# Revit family: Vents_VCUN_Eng
name_source: partatom
category: Mechanical Equipment
units: mm (PartAtom-declared; Revit-internal decimal feet)

## family parameters
Always vertical = Yes
Classification = None
Cut with Voids When Loaded = No
Part Type = Normal
Room Calculation Point = No
Round Connector Dimension = Use Diameter
Shared = No
Work Plane-Based = No

## types (31) — shared parameters
00_20_Manufacturer = Vents
00_20_Name = Centrifugal fan in scroll casing
Casing Material = Metal, painted, blue, matte RAL 5007
Frequency = 50 Hz
Hd = 450 mm
Load Classification = HVAC
Maintenance zone material = <By Category>
Manufacturer = Vents
Number of Fase = 3
Temperature of moving air = 60°С
URL = https://ventilation-system.com
Voltage = 400 V
X2 = 12 mm  [stored 0.0393701 ft]
zero-valued in all types: Default Elevation

## per-type parameters (varying)
- VCUN 500х229-11,0-4: 00_20_Type=VCUN 500х229-11,0-4; Amperage=24 A; B=860 mm; D=500 mm; Diameter=500 mm; F=48 mm  [stored 0.15748 ft]; Frame=Frame VCUN : Frame _500/11; Frame corner=63 mm  [stored 0.206693 ft]; H=1115 mm; H1=390 mm; H2=341 mm; H3=534 mm; Height=1115 mm; Hy=355 mm; L=761 mm; L1=401 mm; L2=353 mm; Length=824 mm; Ly=355 mm; Maximum Air Flow=17250.0 m³/h; Motor=Motor : Motor 11 kW; Power=11000 W; R=250 mm; R1=464 mm; R2=450 mm; R3=340 mm; Weight=107.00 kg; Width=860 mm; X1=483 mm; X3=250 mm; X4=365 mm; Y1=15 mm  [stored 0.0492126 ft]; Y2=330 mm; Y3=190 mm; Y4=531 mm; d=11 mm  [stored 0.0360892 ft]; f=24 mm  [stored 0.0787402 ft]; l=177 mm; r1=31 mm  [stored 0.101706 ft]; r2=145 mm
- VCUN 140х74-0,37-2: 00_20_Type=VCUN 140х74-0,37-2; Amperage=1 A; B=242 mm; D=140 mm; Diameter=140 mm; F=30 mm  [stored 0.0984252 ft]; Frame=Frame VCUN : Frame _140/0.37; Frame corner=35 mm  [stored 0.114829 ft]; H=323 mm; H1=125 mm; H2=92 mm; H3=144 mm; Height=323 mm; Hy=100 mm; L=309 mm; L1=125 mm; L2=95 mm; Length=344 mm; Ly=100 mm; Maximum Air Flow=710.0 m³/h; Motor=Motor : Motor 0.37 kW; Power=370 W; R=70 mm; R1=130 mm; R2=140 mm; R3=100 mm; Weight=9.30 kg; Width=242 mm; X1=130 mm; X3=75 mm; X4=102 mm; Y1=15 mm  [stored 0.0492126 ft]; Y2=95 mm; Y3=57 mm  [stored 0.187008 ft]; Y4=149 mm; d=8 mm  [stored 0.0262467 ft]; f=15 mm  [stored 0.0492126 ft]; l=48 mm  [stored 0.15748 ft]; r1=9 mm  [stored 0.0295276 ft]; r2=39 mm  [stored 0.127953 ft]
- VCUN 160х74-0,55-4: 00_20_Type=VCUN 160х74-0,55-4; Amperage=2 A; B=277 mm; D=160 mm; Diameter=160 mm; F=30 mm  [stored 0.0984252 ft]; Frame=Frame VCUN : Frame _160/0.55; Frame corner=35 mm  [stored 0.114829 ft]; H=373 mm; H1=134 mm; H2=106 mm; H3=173 mm; Height=373 mm; Hy=112 mm; L=356 mm; L1=134 mm; L2=104 mm; Length=391 mm; Ly=112 mm; Maximum Air Flow=750.0 m³/h; Motor=Motor : Motor 0.55 kW; Power=550 W; R=80 mm; R1=150 mm; R2=140 mm; R3=110 mm; Weight=12.70 kg; Width=277 mm; X1=150 mm; X3=85 mm; X4=118 mm; Y1=15 mm  [stored 0.0492126 ft]; Y2=110 mm; Y3=64 mm  [stored 0.209974 ft]; Y4=170 mm; d=8 mm  [stored 0.0262467 ft]; f=15 mm  [stored 0.0492126 ft]; l=52 mm; r1=10 mm  [stored 0.0328084 ft]; r2=42 mm  [stored 0.137795 ft]
- VCUN 160х74-0,75-2: 00_20_Type=VCUN 160х74-0,75-2; Amperage=2 A; B=277 mm; D=160 mm; Diameter=160 mm; F=30 mm  [stored 0.0984252 ft]; Frame=Frame VCUN : Frame _160/0.75; Frame corner=35 mm  [stored 0.114829 ft]; H=373 mm; H1=134 mm; H2=106 mm; H3=173 mm; Height=373 mm; Hy=112 mm; L=356 mm; L1=134 mm; L2=104 mm; Length=391 mm; Ly=112 mm; Maximum Air Flow=1540.0 m³/h; Motor=Motor : Motor 0.75 kW; Power=750 W; R=80 mm; R1=150 mm; R2=140 mm; R3=110 mm; Weight=13.00 kg; Width=277 mm; X1=150 mm; X3=85 mm; X4=118 mm; Y1=15 mm  [stored 0.0492126 ft]; Y2=110 mm; Y3=64 mm  [stored 0.209974 ft]; Y4=170 mm; d=8 mm  [stored 0.0262467 ft]; f=15 mm  [stored 0.0492126 ft]; l=52 mm; r1=10 mm  [stored 0.0328084 ft]; r2=42 mm  [stored 0.137795 ft]
- VCUN 180х74-0,55-4: 00_20_Type=VCUN 180х74-0,55-4; Amperage=2 A; B=311 mm; D=180 mm; Diameter=180 mm; F=29 mm; Frame=Frame VCUN : Frame _180/0.55; Frame corner=40 mm  [stored 0.131234 ft]; H=414 mm; H1=143 mm; H2=120 mm; H3=193 mm; Height=414 mm; Hy=125 mm; L=365 mm; L1=143 mm; L2=114 mm; Length=405 mm; Ly=118 mm; Maximum Air Flow=1030.0 m³/h; Motor=Motor : Motor 0.55 kW; Power=550 W; R=90 mm; R1=170 mm; R2=160 mm; R3=120 mm; Weight=13.50 kg; Width=311 mm; X1=170 mm; X3=85 mm; X4=132 mm; Y1=15 mm  [stored 0.0492126 ft]; Y2=130 mm; Y3=72 mm; Y4=192 mm; d=10 mm  [stored 0.0328084 ft]; f=15 mm  [stored 0.0492126 ft]; l=57 mm  [stored 0.187008 ft]; r1=11 mm  [stored 0.0360892 ft]; r2=46 mm  [stored 0.150919 ft]
- VCUN 180х74-1,1-2: 00_20_Type=VCUN 180х74-0,55-4; Amperage=3 A; B=345 mm; D=180 mm; Diameter=180 mm; F=29 mm; Frame=Frame VCUN : Frame _180/1.1; Frame corner=40 mm  [stored 0.131234 ft]; H=414 mm; H1=143 mm; H2=120 mm; H3=193 mm; Height=414 mm; Hy=125 mm; L=365 mm; L1=143 mm; L2=114 mm; Length=405 mm; Ly=118 mm; Maximum Air Flow=1950.0 m³/h; Motor=Motor : Motor 1.1 kW/200; Power=1100 W; R=90 mm; R1=170 mm; R2=160 mm; R3=120 mm; Weight=14.50 kg; Width=345 mm; X1=170 mm; X3=85 mm; X4=132 mm; Y1=15 mm  [stored 0.0492126 ft]; Y2=130 mm; Y3=72 mm; Y4=192 mm; d=10 mm  [stored 0.0328084 ft]; f=15 mm  [stored 0.0492126 ft]; l=57 mm  [stored 0.187008 ft]; r1=11 mm  [stored 0.0360892 ft]; r2=46 mm  [stored 0.150919 ft]
- VCUN 200х93-0,55-4: 00_20_Type=VCUN 200х93-0,55-4; Amperage=2 A; B=345 mm; D=200 mm; Diameter=200 mm; F=31 mm  [stored 0.101706 ft]; Frame=Frame VCUN : Frame _200/0.55; Frame corner=40 mm  [stored 0.131234 ft]; H=436 mm; H1=160 mm; H2=134 mm; H3=193 mm; Height=436 mm; Hy=125 mm; L=380 mm; L1=160 mm; L2=129 mm; Length=420 mm; Ly=118 mm; Maximum Air Flow=1615.0 m³/h; Motor=Motor : Motor 0.55 kW; Power=550 W; R=100 mm; R1=175 mm; R2=150 mm; R3=150 mm; Weight=15.20 kg; Width=345 mm; X1=170 mm; X3=120 mm; X4=162 mm; Y1=15 mm  [stored 0.0492126 ft]; Y2=140 mm; Y3=79 mm; Y4=213 mm; d=10 mm  [stored 0.0328084 ft]; f=16 mm  [stored 0.0524934 ft]; l=65 mm; r1=13 mm  [stored 0.0426509 ft]; r2=52 mm
- VCUN 200х93-1,1-2: 00_20_Type=VCUN 200х93-1,1-2; Amperage=3 A; B=345 mm; D=200 mm; Diameter=200 mm; F=31 mm  [stored 0.101706 ft]; Frame=Frame VCUN : Frame _200/1.1; Frame corner=40 mm  [stored 0.131234 ft]; H=436 mm; H1=160 mm; H2=134 mm; H3=193 mm; Height=436 mm; Hy=125 mm; L=380 mm; L1=160 mm; L2=129 mm; Length=420 mm; Ly=118 mm; Maximum Air Flow=1900.0 m³/h; Motor=Motor : Motor 1.1 kW/200; Power=1100 W; R=100 mm; R1=175 mm; R2=150 mm; R3=150 mm; Weight=16.20 kg; Width=345 mm; X1=170 mm; X3=120 mm; X4=162 mm; Y1=15 mm  [stored 0.0492126 ft]; Y2=140 mm; Y3=79 mm; Y4=213 mm; d=10 mm  [stored 0.0328084 ft]; f=16 mm  [stored 0.0524934 ft]; l=65 mm; r1=13 mm  [stored 0.0426509 ft]; r2=52 mm
- VCUN 225х103-1,1-4: 00_20_Type=VCUN 225х103-1,1-4; Amperage=3 A; B=388 mm; D=225 mm; Diameter=225 mm; F=31 mm  [stored 0.101706 ft]; Frame=Frame VCUN : Frame _225/1.1; Frame corner=45 mm  [stored 0.147638 ft]; H=507 mm; H1=178 mm; H2=151 mm; H3=232 mm; Height=507 mm; Hy=160 mm; L=432 mm; L1=172 mm; L2=141 mm; Length=477 mm; Ly=150 mm; Maximum Air Flow=2125.0 m³/h; Motor=Motor : Motor 1.1 kW; Power=1100 W; R=113 mm; R1=200 mm; R2=180 mm; R3=150 mm; Weight=21.20 kg; Width=388 mm; X1=170 mm; X3=120 mm; X4=204 mm; Y1=15 mm  [stored 0.0492126 ft]; Y2=140 mm; Y3=94 mm; Y4=245 mm; d=10 mm  [stored 0.0328084 ft]; f=16 mm  [stored 0.0524934 ft]; l=71 mm; r1=14 mm  [stored 0.0459318 ft]; r2=56 mm
- VCUN 225х103-2,2-2: 00_20_Type=VCUN 225х103-2,2-2; Amperage=5 A; B=388 mm; D=225 mm; Diameter=225 mm; F=31 mm  [stored 0.101706 ft]; Frame=Frame VCUN : Frame _225/2.2; Frame corner=45 mm  [stored 0.147638 ft]; H=507 mm; H1=178 mm; H2=151 mm; H3=232 mm; Height=507 mm; Hy=160 mm; L=432 mm; L1=172 mm; L2=141 mm; Length=477 mm; Ly=150 mm; Maximum Air Flow=3350.0 m³/h; Motor=Motor : Motor 2.2 kW/225; Power=2200 W; R=113 mm; R1=200 mm; R2=180 mm; R3=150 mm; Weight=24.20 kg; Width=388 mm; X1=170 mm; X3=120 mm; X4=204 mm; Y1=15 mm  [stored 0.0492126 ft]; Y2=140 mm; Y3=94 mm; Y4=245 mm; d=10 mm  [stored 0.0328084 ft]; f=16 mm  [stored 0.0524934 ft]; l=71 mm; r1=14 mm  [stored 0.0459318 ft]; r2=56 mm
- VCUN 240х114-2,2-4: 00_20_Type=VCUN 240х114-2,2-4; Amperage=5 A; B=414 mm; D=240 mm; Diameter=240 mm; F=30 mm  [stored 0.0984252 ft]; Frame=Frame VCUN : Frame _240/2.2; Frame corner=45 mm  [stored 0.147638 ft]; H=568 mm; H1=186 mm; H2=161 mm; H3=282 mm; Height=568 mm; Hy=170 mm; L=461 mm; L1=186 mm; L2=156 mm; Length=506 mm; Ly=160 mm; Maximum Air Flow=2930.0 m³/h; Motor=Motor : Motor 2.2 kW/280; Power=2200 W; R=120 mm; R1=210 mm; R2=210 mm; R3=160 mm; Weight=30.50 kg; Width=414 mm; X1=200 mm; X3=130 mm; X4=200 mm; Y1=15 mm  [stored 0.0492126 ft]; Y2=160 mm; Y3=95 mm; Y4=256 mm; d=10 mm  [stored 0.0328084 ft]; f=15 mm  [stored 0.0492126 ft]; l=78 mm; r1=15 mm  [stored 0.0492126 ft]; r2=63 mm  [stored 0.206693 ft]
- VCUN 240х114-3,0-2: 00_20_Type=VCUN 240х114-3,0-2; Amperage=6 A; B=414 mm; D=240 mm; Diameter=240 mm; F=30 mm  [stored 0.0984252 ft]; Frame=Frame VCUN : Frame _240/3; Frame corner=45 mm  [stored 0.147638 ft]; H=568 mm; H1=186 mm; H2=161 mm; H3=282 mm; Height=568 mm; Hy=170 mm; L=461 mm; L1=186 mm; L2=156 mm; Length=506 mm; Ly=160 mm; Maximum Air Flow=4350.0 m³/h; Motor=Motor : Motor 3 kW/240; Power=3000 W; R=120 mm; R1=210 mm; R2=210 mm; R3=160 mm; Weight=31.40 kg; Width=414 mm; X1=200 mm; X3=130 mm; X4=200 mm; Y1=15 mm  [stored 0.0492126 ft]; Y2=160 mm; Y3=95 mm; Y4=256 mm; d=10 mm  [stored 0.0328084 ft]; f=15 mm  [stored 0.0492126 ft]; l=78 mm; r1=15 mm  [stored 0.0492126 ft]; r2=63 mm  [stored 0.206693 ft]
- VCUN 250х127-1,5-6: 00_20_Type=VCUN 250х127-1,5-6; Amperage=4 A; B=431 mm; D=250 mm; Diameter=250 mm; F=36 mm  [stored 0.11811 ft]; Frame=Frame VCUN : Frame _250/1.5; Frame corner=50 mm  [stored 0.164042 ft]; H=594 mm; H1=202 mm; H2=168 mm; H3=292 mm; Height=594 mm; Hy=170 mm; L=473 mm; L1=202 mm; L2=166 mm; Length=523 mm; Ly=170 mm; Maximum Air Flow=2415.0 m³/h; Motor=Motor : Motor 1.5 kW/280; Power=1500 W; R=125 mm; R1=210 mm; R2=210 mm; R3=165 mm; Weight=33.00 kg; Width=431 mm; X1=200 mm; X3=130 mm; X4=214 mm; Y1=15 mm  [stored 0.0492126 ft]; Y2=160 mm; Y3=98 mm; Y4=266 mm; d=10 mm  [stored 0.0328084 ft]; f=18 mm  [stored 0.0590551 ft]; l=83 mm; r1=16 mm  [stored 0.0524934 ft]; r2=67 mm
- VCUN 250х127-2,2-4: 00_20_Type=VCUN 250х127-2,2-4; Amperage=5 A; B=431 mm; D=250 mm; Diameter=250 mm; F=36 mm  [stored 0.11811 ft]; Frame=Frame VCUN : Frame _250/2.2; Frame corner=50 mm  [stored 0.164042 ft]; H=594 mm; H1=202 mm; H2=168 mm; H3=292 mm; Height=594 mm; Hy=170 mm; L=473 mm; L1=202 mm; L2=166 mm; Length=523 mm; Ly=170 mm; Maximum Air Flow=3720.0 m³/h; Motor=Motor : Motor 2.2 kW/280; Power=2200 W; R=125 mm; R1=210 mm; R2=210 mm; R3=165 mm; Weight=32.20 kg; Width=431 mm; X1=200 mm; X3=130 mm; X4=214 mm; Y1=15 mm  [stored 0.0492126 ft]; Y2=160 mm; Y3=98 mm; Y4=266 mm; d=10 mm  [stored 0.0328084 ft]; f=18 mm  [stored 0.0590551 ft]; l=83 mm; r1=16 mm  [stored 0.0524934 ft]; r2=67 mm
- VCUN 250х127-5,5-2: 00_20_Type=VCUN 250х127-5,5-2; Amperage=11 A; B=431 mm; D=250 mm; Diameter=250 mm; F=36 mm  [stored 0.11811 ft]; Frame=Frame VCUN : Frame _250/5.5; Frame corner=50 mm  [stored 0.164042 ft]; H=614 mm; H1=202 mm; H2=168 mm; H3=312 mm; Height=614 mm; Hy=170 mm; L=517 mm; L1=202 mm; L2=166 mm; Length=567 mm; Ly=170 mm; Maximum Air Flow=4820.0 m³/h; Motor=Motor : Motor 5.5 kW/280; Power=5500 W; R=125 mm; R1=210 mm; R2=210 mm; R3=165 mm; Weight=40.00 kg; Width=431 mm; X1=200 mm; X3=130 mm; X4=214 mm; Y1=15 mm  [stored 0.0492126 ft]; Y2=160 mm; Y3=98 mm; Y4=266 mm; d=10 mm  [stored 0.0328084 ft]; f=18 mm  [stored 0.0590551 ft]; l=83 mm; r1=16 mm  [stored 0.0524934 ft]; r2=67 mm
- VCUN 280х127-1,5-6: 00_20_Type=VCUN 280х127-1,5-6; Amperage=4 A; B=483 mm; D=280 mm; Diameter=280 mm; F=35 mm  [stored 0.114829 ft]; Frame=Frame VCUN : Frame _280/1.5; Frame corner=50 mm  [stored 0.164042 ft]; H=626 mm; H1=225 mm; H2=189 mm; H3=292 mm; Height=626 mm; Hy=190 mm; L=503 mm; L1=231 mm; L2=196 mm; Length=553 mm; Ly=200 mm; Maximum Air Flow=3450.0 m³/h; Motor=Motor : Motor 1.5 kW/280; Power=1500 W; R=140 mm; R1=260 mm; R2=250 mm; R3=180 mm; Weight=35.10 kg; Width=483 mm; X1=250 mm; X3=130 mm; X4=222 mm; Y1=15 mm  [stored 0.0492126 ft]; Y2=180 mm; Y3=110 mm; Y4=299 mm; d=10 mm  [stored 0.0328084 ft]; f=18 mm  [stored 0.0590551 ft]; l=98 mm; r1=18 mm  [stored 0.0590551 ft]; r2=81 mm
- VCUN 280х127-2,2-4: 00_20_Type=VCUN 280х127-2,2-4; Amperage=5 A; B=483 mm; D=280 mm; Diameter=280 mm; F=35 mm  [stored 0.114829 ft]; Frame=Frame VCUN : Frame _280/2.2; Frame corner=50 mm  [stored 0.164042 ft]; H=626 mm; H1=225 mm; H2=189 mm; H3=292 mm; Height=626 mm; Hy=190 mm; L=503 mm; L1=231 mm; L2=196 mm; Length=553 mm; Ly=200 mm; Maximum Air Flow=4395.0 m³/h; Motor=Motor : Motor 2.2 kW/280; Power=2200 W; R=140 mm; R1=260 mm; R2=250 mm; R3=180 mm; Weight=34.20 kg; Width=483 mm; X1=250 mm; X3=130 mm; X4=222 mm; Y1=15 mm  [stored 0.0492126 ft]; Y2=180 mm; Y3=110 mm; Y4=299 mm; d=10 mm  [stored 0.0328084 ft]; f=18 mm  [stored 0.0590551 ft]; l=98 mm; r1=18 mm  [stored 0.0590551 ft]; r2=81 mm
- VCUN 280х127-5,5-2: 00_20_Type=VCUN 280х127-5,5-2; Amperage=11 A; B=483 mm; D=280 mm; Diameter=280 mm; F=35 mm  [stored 0.114829 ft]; Frame=Frame VCUN : Frame _280/5.5; Frame corner=50 mm  [stored 0.164042 ft]; H=646 mm; H1=225 mm; H2=189 mm; H3=312 mm; Height=646 mm; Hy=190 mm; L=545 mm; L1=231 mm; L2=196 mm; Length=595 mm; Ly=200 mm; Maximum Air Flow=6330.0 m³/h; Motor=Motor : Motor 5.5 kW/280; Power=5500 W; R=140 mm; R1=260 mm; R2=250 mm; R3=180 mm; Weight=42.40 kg; Width=483 mm; X1=250 mm; X3=130 mm; X4=222 mm; Y1=15 mm  [stored 0.0492126 ft]; Y2=180 mm; Y3=110 mm; Y4=299 mm; d=10 mm  [stored 0.0328084 ft]; f=18 mm  [stored 0.0590551 ft]; l=98 mm; r1=18 mm  [stored 0.0590551 ft]; r2=81 mm
- VCUN 315х143-2,2-6: 00_20_Type=VCUN 315х143-2,2-6; Amperage=6 A; B=543 mm; D=315 mm; Diameter=315 mm; F=39 mm  [stored 0.127953 ft]; Frame=Frame VCUN : Frame _315/2.2; Frame corner=50 mm  [stored 0.164042 ft]; H=731 mm; H1=250 mm; H2=213 mm; H3=353 mm; Height=731 mm; Hy=224 mm; L=568 mm; L1=255 mm; L2=216 mm; Length=618 mm; Ly=224 mm; Maximum Air Flow=4375.0 m³/h; Motor=Motor : Motor 2.2 kW; Power=2200 W; R=158 mm; R1=300 mm; R2=240 mm; R3=200 mm; Weight=46.80 kg; Width=543 mm; X1=260 mm; X3=150 mm; X4=273 mm; Y1=15 mm  [stored 0.0492126 ft]; Y2=200 mm; Y3=126 mm; Y4=339 mm; d=10 mm  [stored 0.0328084 ft]; f=20 mm  [stored 0.0656168 ft]; l=108 mm; r1=20 mm  [stored 0.0656168 ft]; r2=88 mm
- VCUN 315х143-4,0-4: 00_20_Type=VCUN 315х143-4,0-4; Amperage=9 A; B=543 mm; D=315 mm; Diameter=315 mm; F=39 mm  [stored 0.127953 ft]; Frame=Frame VCUN : Frame _315/4; Frame corner=50 mm  [stored 0.164042 ft]; H=731 mm; H1=250 mm; H2=213 mm; H3=353 mm; Height=731 mm; Hy=224 mm; L=568 mm; L1=255 mm; L2=216 mm; Length=618 mm; Ly=224 mm; Maximum Air Flow=6530.0 m³/h; Motor=Motor : Motor 4 kW/355; Power=4000 W; R=158 mm; R1=300 mm; R2=240 mm; R3=200 mm; Weight=49.80 kg; Width=543 mm; X1=260 mm; X3=150 mm; X4=273 mm; Y1=15 mm  [stored 0.0492126 ft]; Y2=200 mm; Y3=126 mm; Y4=339 mm; d=10 mm  [stored 0.0328084 ft]; f=20 mm  [stored 0.0656168 ft]; l=108 mm; r1=20 mm  [stored 0.0656168 ft]; r2=88 mm
- VCUN 355х143-2,2-6: 00_20_Type=VCUN 355х143-2,2-6; Amperage=6 A; B=611 mm; D=355 mm; Diameter=355 mm; F=41 mm  [stored 0.134514 ft]; Frame=Frame VCUN : Frame _355/2.2; Frame corner=50 mm  [stored 0.164042 ft]; H=817 mm; H1=275 mm; H2=241 mm; H3=403 mm; Height=817 mm; Hy=250 mm; L=566 mm; L1=255 mm; L2=214 mm; Length=616 mm; Ly=224 mm; Maximum Air Flow=5090.0 m³/h; Motor=Motor : Motor 2.2 kW; Power=2200 W; R=178 mm; R1=300 mm; R2=280 mm; R3=225 mm; Weight=49.00 kg; Width=611 mm; X1=280 mm; X3=180 mm; X4=317 mm; Y1=0 mm  [stored 0 ft]; Y2=230 mm; Y3=132 mm; Y4=373 mm; d=10 mm  [stored 0.0328084 ft]; f=21 mm  [stored 0.0688976 ft]; l=107 mm; r1=22 mm  [stored 0.0721785 ft]; r2=85 mm
- VCUN 355х143-4,0-4: 00_20_Type=VCUN 355х143-4,0-4; Amperage=9 A; B=611 mm; D=355 mm; Diameter=355 mm; F=41 mm  [stored 0.134514 ft]; Frame=Frame VCUN : Frame _355/4; Frame corner=50 mm  [stored 0.164042 ft]; H=817 mm; H1=275 mm; H2=241 mm; H3=403 mm; Height=817 mm; Hy=250 mm; L=566 mm; L1=255 mm; L2=214 mm; Length=616 mm; Ly=224 mm; Maximum Air Flow=8150.0 m³/h; Motor=Motor : Motor 4 kW/355; Power=4000 W; R=178 mm; R1=300 mm; R2=280 mm; R3=225 mm; Weight=51.00 kg; Width=611 mm; X1=280 mm; X3=180 mm; X4=317 mm; Y1=0 mm  [stored 0 ft]; Y2=230 mm; Y3=132 mm; Y4=373 mm; d=10 mm  [stored 0.0328084 ft]; f=21 mm  [stored 0.0688976 ft]; l=107 mm; r1=22 mm  [stored 0.0721785 ft]; r2=85 mm
- VCUN 400х183-1,5-8: 00_20_Type=VCUN 400х183-1,5-8; Amperage=4 A; B=689 mm; D=400 mm; Diameter=400 mm; F=42 mm  [stored 0.137795 ft]; Frame=Frame VCUN : Frame _400/1.5; Frame corner=50 mm  [stored 0.164042 ft]; H=870 mm; H1=310 mm; H2=272 mm; H3=403 mm; Height=870 mm; Hy=280 mm; L=619 mm; L1=310 mm; L2=268 mm; Length=669 mm; Ly=280 mm; Maximum Air Flow=6545.0 m³/h; Motor=Motor : Motor 1.5 kW; Power=1500 W; R=200 mm; R1=340 mm; R2=320 mm; R3=260 mm; Weight=57.10 kg; Width=689 mm; X1=320 mm; X3=210 mm; X4=343 mm; Y1=60 mm  [stored 0.19685 ft]; Y2=280 mm; Y3=126 mm; Y4=398 mm; d=10 mm  [stored 0.0328084 ft]; f=21 mm  [stored 0.0688976 ft]; l=134 mm; r1=25 mm  [stored 0.082021 ft]; r2=109 mm
- VCUN 400х183-2,2-6: 00_20_Type=VCUN 400х183-2,2-6; Amperage=6 A; B=689 mm; D=400 mm; Diameter=400 mm; F=42 mm  [stored 0.137795 ft]; Frame=Frame VCUN : Frame _400/2.2; Frame corner=50 mm  [stored 0.164042 ft]; H=870 mm; H1=310 mm; H2=272 mm; H3=403 mm; Height=870 mm; Hy=280 mm; L=619 mm; L1=310 mm; L2=268 mm; Length=669 mm; Ly=280 mm; Maximum Air Flow=8100.0 m³/h; Motor=Motor : Motor 2.2 kW; Power=2200 W; R=200 mm; R1=340 mm; R2=320 mm; R3=260 mm; Weight=54.10 kg; Width=689 mm; X1=320 mm; X3=210 mm; X4=343 mm; Y1=60 mm  [stored 0.19685 ft]; Y2=280 mm; Y3=126 mm; Y4=398 mm; d=10 mm  [stored 0.0328084 ft]; f=21 mm  [stored 0.0688976 ft]; l=134 mm; r1=25 mm  [stored 0.082021 ft]; r2=109 mm
- VCUN 400х183-5,5-4: 00_20_Type=VCUN 400х183-5,5-4; Amperage=11 A; B=689 mm; D=400 mm; Diameter=400 mm; F=41 mm  [stored 0.134514 ft]; Frame=Frame VCUN : Frame _400/5.5; Frame corner=50 mm  [stored 0.164042 ft]; H=882 mm; H1=310 mm; H2=272 mm; H3=414 mm; Height=882 mm; Hy=280 mm; L=662 mm; L1=330 mm; L2=289 mm; Length=712 mm; Ly=300 mm; Maximum Air Flow=10175.0 m³/h; Motor=Motor : Motor 5.5kW/400; Power=5500 W; R=200 mm; R1=360 mm; R2=320 mm; R3=275 mm; Weight=69.50 kg; Width=689 mm; X1=320 mm; X3=210 mm; X4=341 mm; Y1=60 mm  [stored 0.19685 ft]; Y2=280 mm; Y3=155 mm; Y4=427 mm; d=10 mm  [stored 0.0328084 ft]; f=21 mm  [stored 0.0688976 ft]; l=145 mm; r1=25 mm  [stored 0.082021 ft]; r2=120 mm
- VCUN 450х203-3,0-8: 00_20_Type=VCUN 450х203-3,0-8; Amperage=8 A; B=774 mm; D=450 mm; Diameter=450 mm; F=37 mm  [stored 0.121391 ft]; Frame=Frame VCUN : Frame _450/3; Frame corner=63 mm  [stored 0.206693 ft]; H=985 mm; H1=345 mm; H2=306 mm; H3=464 mm; Height=985 mm; Hy=315 mm; L=690 mm; L1=352 mm; L2=315 mm; Length=753 mm; Ly=315 mm; Maximum Air Flow=10230.0 m³/h; Motor=Motor : Motor 3 kW; Power=3000 W; R=225 mm; R1=400 mm; R2=360 mm; R3=300 mm; Weight=77.80 kg; Width=774 mm; X1=350 mm; X3=240 mm; X4=392 mm; Y1=60 mm  [stored 0.19685 ft]; Y2=310 mm; Y3=178 mm; Y4=484 mm; d=10 mm  [stored 0.0328084 ft]; f=19 mm; l=158 mm; r1=28 mm; r2=129 mm
- VCUN 450х203-4,0-6: 00_20_Type=VCUN 450х203-4,0-6; Amperage=9 A; B=774 mm; D=450 mm; Diameter=450 mm; F=37 mm  [stored 0.121391 ft]; Frame=Frame VCUN : Frame _450/4; Frame corner=63 mm  [stored 0.206693 ft]; H=985 mm; H1=345 mm; H2=306 mm; H3=464 mm; Height=985 mm; Hy=315 mm; L=690 mm; L1=352 mm; L2=315 mm; Length=753 mm; Ly=315 mm; Maximum Air Flow=11150.0 m³/h; Motor=Motor : Motor 4 кВт; Power=4000 W; R=225 mm; R1=400 mm; R2=360 mm; R3=300 mm; Weight=76.50 kg; Width=774 mm; X1=350 mm; X3=240 mm; X4=392 mm; Y1=60 mm  [stored 0.19685 ft]; Y2=310 mm; Y3=178 mm; Y4=484 mm; d=10 mm  [stored 0.0328084 ft]; f=19 mm; l=158 mm; r1=28 mm; r2=129 mm
- VCUN 450х203-11,0-4: 00_20_Type=VCUN 450х203-11,0-4; Amperage=24 A; B=774 mm; D=450 mm; Diameter=450 mm; F=37 mm  [stored 0.121391 ft]; Frame=Frame VCUN : Frame _450/11; Frame corner=63 mm  [stored 0.206693 ft]; H=1005 mm; H1=345 mm; H2=306 mm; H3=484 mm; Height=1005 mm; Hy=315 mm; L=722 mm; L1=352 mm; L2=315 mm; Length=785 mm; Ly=315 mm; Maximum Air Flow=19000.0 m³/h; Motor=Motor : Motor 11 kW; Power=11000 W; R=225 mm; R1=400 mm; R2=360 mm; R3=300 mm; Weight=105.00 kg; Width=774 mm; X1=350 mm; X3=240 mm; X4=392 mm; Y1=60 mm  [stored 0.19685 ft]; Y2=310 mm; Y3=178 mm; Y4=484 mm; d=10 mm  [stored 0.0328084 ft]; f=19 mm; l=158 mm; r1=28 mm; r2=129 mm
- VCUN 500х229-5,5-8: 00_20_Type=VCUN 500х229-5,5-8; Amperage=15 A; B=860 mm; D=500 mm; Diameter=500 mm; F=48 mm  [stored 0.15748 ft]; Frame=Frame VCUN : Frame _500/5.5; Frame corner=63 mm  [stored 0.206693 ft]; H=1115 mm; H1=390 mm; H2=341 mm; H3=534 mm; Height=1115 mm; Hy=355 mm; L=761 mm; L1=401 mm; L2=353 mm; Length=824 mm; Ly=355 mm; Maximum Air Flow=11550.0 m³/h; Motor=Motor : Motor 5.5 kW; Power=5500 W; R=250 mm; R1=464 mm; R2=450 mm; R3=340 mm; Weight=85.00 kg; Width=860 mm; X1=483 mm; X3=250 mm; X4=365 mm; Y1=15 mm  [stored 0.0492126 ft]; Y2=330 mm; Y3=190 mm; Y4=531 mm; d=11 mm  [stored 0.0360892 ft]; f=24 mm  [stored 0.0787402 ft]; l=177 mm; r1=31 mm  [stored 0.101706 ft]; r2=145 mm
- VCUN 500х229-7,5-6: 00_20_Type=VCUN 500х229-7,5-6; Amperage=17 A; B=860 mm; D=500 mm; Diameter=500 mm; F=48 mm  [stored 0.15748 ft]; Frame=Frame VCUN : Frame _500/7.5; Frame corner=63 mm  [stored 0.206693 ft]; H=1115 mm; H1=390 mm; H2=341 mm; H3=534 mm; Height=1115 mm; Hy=355 mm; L=761 mm; L1=401 mm; L2=353 mm; Length=824 mm; Ly=355 mm; Maximum Air Flow=14960.0 m³/h; Motor=Motor : Motor 7.5 kW; Power=7500 W; R=250 mm; R1=464 mm; R2=450 mm; R3=340 mm; Weight=86.00 kg; Width=860 mm; X1=483 mm; X3=250 mm; X4=365 mm; Y1=15 mm  [stored 0.0492126 ft]; Y2=330 mm; Y3=190 mm; Y4=531 mm; d=11 mm  [stored 0.0360892 ft]; f=24 mm  [stored 0.0787402 ft]; l=177 mm; r1=31 mm  [stored 0.101706 ft]; r2=145 mm
- VCUN 140х74-0,25-4: 00_20_Type=VCUN 140х74-0,25-4; Amperage=1 A; B=242 mm; D=140 mm; Diameter=140 mm; F=30 mm  [stored 0.0984252 ft]; Frame=Frame VCUN : Frame _140/0.25; Frame corner=35 mm  [stored 0.114829 ft]; H=323 mm; H1=125 mm; H2=92 mm; H3=144 mm; Height=323 mm; Hy=100 mm; L=309 mm; L1=125 mm; L2=95 mm; Length=344 mm; Ly=100 mm; Maximum Air Flow=450.0 m³/h; Motor=Motor : Motor 0.25 kW; Power=250 W; R=70 mm; R1=130 mm; R2=140 mm; R3=100 mm; Weight=9.30 kg; Width=242 mm; X1=130 mm; X3=75 mm; X4=102 mm; Y1=15 mm  [stored 0.0492126 ft]; Y2=95 mm; Y3=57 mm  [stored 0.187008 ft]; Y4=149 mm; d=8 mm  [stored 0.0262467 ft]; f=15 mm  [stored 0.0492126 ft]; l=48 mm  [stored 0.15748 ft]; r1=9 mm  [stored 0.0295276 ft]; r2=39 mm  [stored 0.127953 ft]

note: [stored X ft] marks values corroborated as IEEE doubles in the binary element streams (Revit-internal decimal feet)
